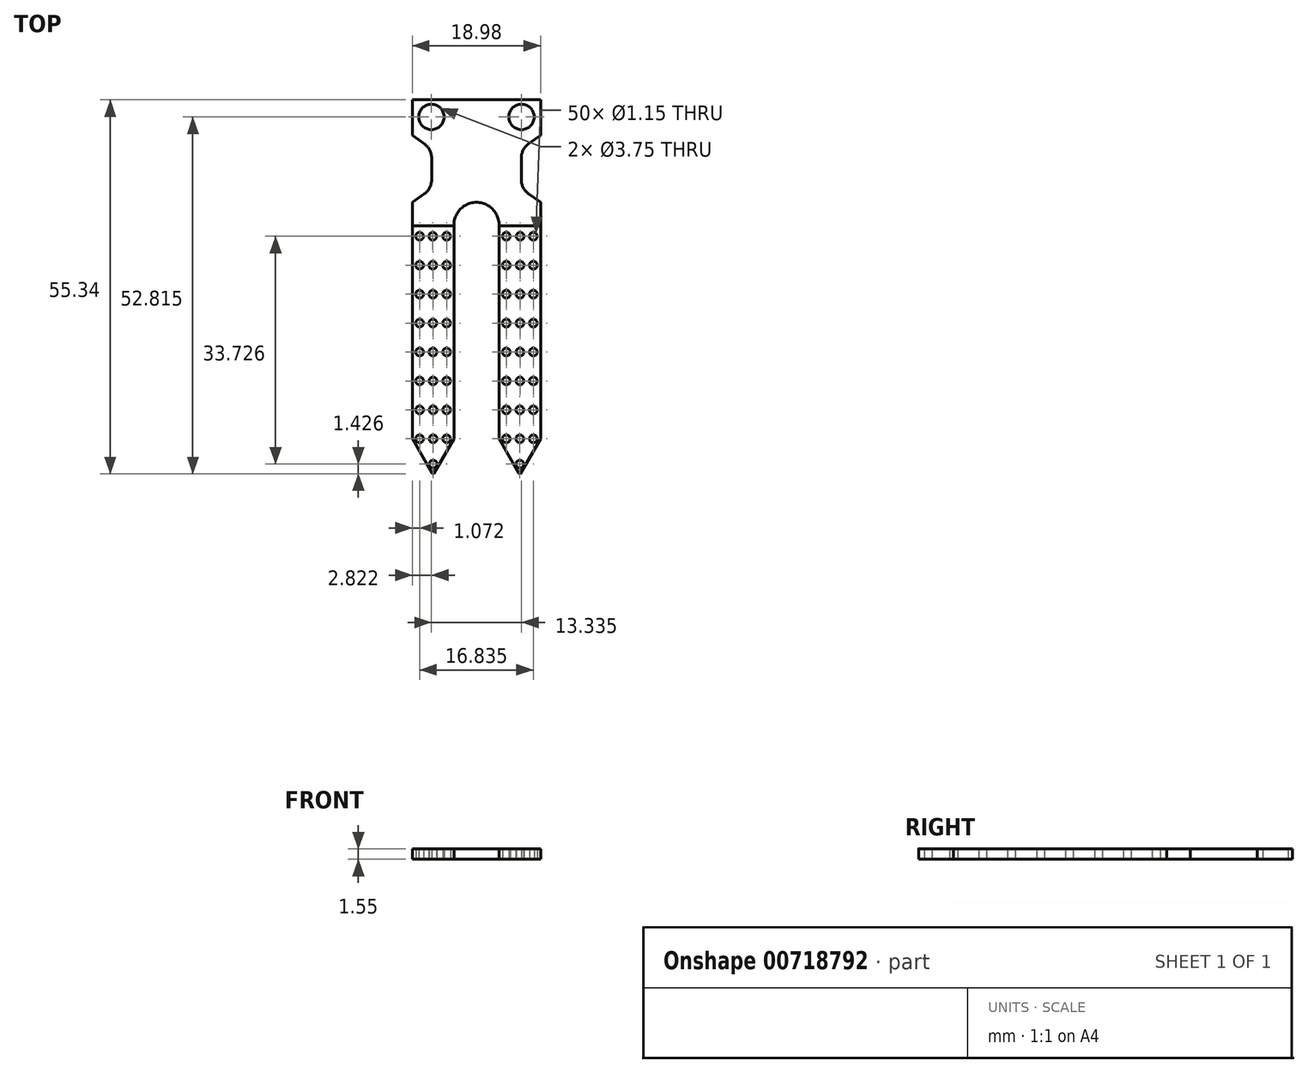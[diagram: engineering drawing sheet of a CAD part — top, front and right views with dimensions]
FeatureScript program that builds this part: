
annotation { "Feature Type Name" : "Feature", "Feature Type Description" : "" }
export const myFeature = defineFeature(function(context is Context, id is Id, definition is map)
    precondition{}
    {
        {
            var Q0;
            Q0=qCreatedBy(makeId("Top.planeOp"),FACE);
            var sketch = newSketch(context, id + "F0", { "sketchPlane" : qUnion([Q0])});
            skLineSegment(sketch, "E0", {"start": v(-9.5, 0) * mm, "end": v(9.5, 0) * mm});
            skLineSegment(sketch, "E1", {"start": v(9.5, 0) * mm, "end": v(9.5, -5.25) * mm});
            skLineSegment(sketch, "E2", {"start": v(9.5, -5.25) * mm, "end": v(6.64, -7.28) * mm});
            skLineSegment(sketch, "E3", {"start": v(6.64, -7.28) * mm, "end": v(6.64, -13.13) * mm});
            skLineSegment(sketch, "E4", {"start": v(6.64, -13.13) * mm, "end": v(9.5, -15.16) * mm});
            skLineSegment(sketch, "E5", {"start": v(9.5, -50.16) * mm, "end": v(6.42, -55.49) * mm});
            skLineSegment(sketch, "E6", {"start": v(6.42, -55.49) * mm, "end": v(3.34, -50.16) * mm});
            skLineSegment(sketch, "E7", {"start": v(9.5, -50.16) * mm, "end": v(3.34, -50.16) * mm, "construction": true});
            skLineSegment(sketch, "E8", {"start": v(6.42, -55.49) * mm, "end": v(6.42, -50.16) * mm, "construction": true});
            skLineSegment(sketch, "E9", {"start": v(9.5, -15.16) * mm, "end": v(9.5, -18.61) * mm});
            skLineSegment(sketch, "E10", {"start": v(9.5, -18.61) * mm, "end": v(9.5, -50.16) * mm});
            skLineSegment(sketch, "E11", {"start": v(3.34, -50.16) * mm, "end": v(3.34, -18.61) * mm});
            skLineSegment(sketch, "E12", {"start": v(3.34, -18.61) * mm, "end": v(9.5, -18.61) * mm});
            skLineSegment(sketch, "E13", {"start": v(0, 0) * mm, "end": v(0, -55.81) * mm, "construction": true});
            skLineSegment(sketch, "E14.MirrorCS", {"start": v(-9.5, -15.16) * mm, "end": v(-9.5, -18.61) * mm});
            skLineSegment(sketch, "E15.MirrorCS", {"start": v(-9.5, -18.61) * mm, "end": v(-9.5, -50.16) * mm});
            skLineSegment(sketch, "E16.MirrorCS", {"start": v(-6.64, -7.28) * mm, "end": v(-6.64, -13.13) * mm});
            skLineSegment(sketch, "E17.MirrorCS", {"start": v(-9.5, -5.25) * mm, "end": v(-6.64, -7.28) * mm});
            skLineSegment(sketch, "E18.MirrorCS", {"start": v(-9.5, 0) * mm, "end": v(-9.5, -5.25) * mm});
            skLineSegment(sketch, "E19.MirrorCS", {"start": v(-6.64, -13.13) * mm, "end": v(-9.5, -15.16) * mm});
            skLineSegment(sketch, "E20.MirrorCS", {"start": v(-6.42, -55.49) * mm, "end": v(-3.34, -50.16) * mm});
            skLineSegment(sketch, "E21.MirrorCS", {"start": v(-9.5, -50.16) * mm, "end": v(-6.42, -55.49) * mm});
            skLineSegment(sketch, "E22.MirrorCS", {"start": v(-3.34, -50.16) * mm, "end": v(-3.34, -18.61) * mm});
            skLineSegment(sketch, "E23.MirrorCS", {"start": v(-3.34, -18.61) * mm, "end": v(-9.5, -18.61) * mm});
            skLineSegment(sketch, "E24", {"start": v(-3.34, -18.61) * mm, "end": v(3.34, -18.61) * mm, "construction": true});
            skLineSegment(sketch, "E25", {"start": v(-9.5, -15.16) * mm, "end": v(9.5, -15.16) * mm, "construction": true});
            skArc(sketch, "E26", {"start": v(3.34, -18.61) * mm, "mid": v(0, -15.16) * mm, "end": v(-3.34, -18.61) * mm});
            skLineSegment(sketch, "E27.MirrorCS", {"start": v(-9.5, -50.16) * mm, "end": v(-3.34, -50.16) * mm, "construction": true});
            skLineSegment(sketch, "E28.MirrorCS", {"start": v(-6.42, -55.49) * mm, "end": v(-6.42, -50.16) * mm, "construction": true});
            skCircle(sketch, "E29", {"center": v(6.67, -2.52) * mm, "radius": 1.88 * mm});
            skCircle(sketch, "E30.MirrorC", {"center": v(-6.67, -2.52) * mm, "radius": 1.88 * mm});
            skCircle(sketch, "E31", {"center": v(4.42, -20.19) * mm, "radius": 0.57 * mm});
            skCircle(sketch, "E32", {"center": v(6.47, -20.19) * mm, "radius": 0.57 * mm});
            skCircle(sketch, "E33", {"center": v(8.42, -20.19) * mm, "radius": 0.57 * mm});
            skLineSegment(sketch, "E34", {"start": v(3.34, -20.19) * mm, "end": v(9.5, -20.19) * mm, "construction": true});
            skCircle(sketch, "E35", {"center": v(6.42, -53.91) * mm, "radius": 0.57 * mm});
            skCircle(sketch, "E36", {"center": v(4.42, -50.16) * mm, "radius": 0.57 * mm});
            skCircle(sketch, "E37", {"center": v(6.42, -50.16) * mm, "radius": 0.57 * mm});
            skCircle(sketch, "E38", {"center": v(8.42, -50.16) * mm, "radius": 0.57 * mm});
            skLineSegment(sketch, "E39", {"start": v(4.42, -50.16) * mm, "end": v(4.42, -20.19) * mm, "construction": true});
            skLineSegment(sketch, "E40", {"start": v(6.42, -50.16) * mm, "end": v(6.47, -20.19) * mm, "construction": true});
            skLineSegment(sketch, "E41", {"start": v(8.42, -20.19) * mm, "end": v(8.42, -50.16) * mm, "construction": true});
            skLineSegment(sketch, "E42", {"start": v(3.34, -41.6) * mm, "end": v(9.5, -41.6) * mm, "construction": true});
            skLineSegment(sketch, "E43", {"start": v(3.34, -37.32) * mm, "end": v(9.5, -37.32) * mm, "construction": true});
            skLineSegment(sketch, "E44", {"start": v(3.34, -33.03) * mm, "end": v(9.5, -33.03) * mm, "construction": true});
            skLineSegment(sketch, "E45", {"start": v(3.34, -28.75) * mm, "end": v(9.5, -28.75) * mm, "construction": true});
            skLineSegment(sketch, "E46", {"start": v(3.34, -24.47) * mm, "end": v(9.5, -24.47) * mm, "construction": true});
            skCircle(sketch, "E47", {"center": v(4.42, -24.47) * mm, "radius": 0.57 * mm});
            skCircle(sketch, "E48", {"center": v(6.46, -24.47) * mm, "radius": 0.57 * mm});
            skCircle(sketch, "E49", {"center": v(8.42, -24.47) * mm, "radius": 0.57 * mm});
            skCircle(sketch, "E50", {"center": v(4.42, -28.75) * mm, "radius": 0.57 * mm});
            skCircle(sketch, "E51", {"center": v(6.45, -28.75) * mm, "radius": 0.57 * mm});
            skCircle(sketch, "E52", {"center": v(8.42, -28.75) * mm, "radius": 0.57 * mm});
            skLineSegment(sketch, "E53", {"start": v(3.34, -45.88) * mm, "end": v(9.5, -45.88) * mm, "construction": true});
            skCircle(sketch, "E54", {"center": v(4.42, -33.03) * mm, "radius": 0.57 * mm});
            skCircle(sketch, "E55", {"center": v(6.45, -33.03) * mm, "radius": 0.57 * mm});
            skCircle(sketch, "E56", {"center": v(8.42, -33.03) * mm, "radius": 0.57 * mm});
            skCircle(sketch, "E57", {"center": v(4.42, -37.32) * mm, "radius": 0.57 * mm});
            skCircle(sketch, "E58", {"center": v(6.44, -37.32) * mm, "radius": 0.57 * mm});
            skCircle(sketch, "E59", {"center": v(8.42, -37.32) * mm, "radius": 0.57 * mm});
            skCircle(sketch, "E60", {"center": v(4.42, -41.6) * mm, "radius": 0.57 * mm});
            skCircle(sketch, "E61", {"center": v(6.43, -41.6) * mm, "radius": 0.57 * mm});
            skCircle(sketch, "E62", {"center": v(8.42, -41.6) * mm, "radius": 0.57 * mm});
            skCircle(sketch, "E63", {"center": v(4.42, -45.88) * mm, "radius": 0.57 * mm});
            skCircle(sketch, "E64", {"center": v(6.42, -45.88) * mm, "radius": 0.57 * mm});
            skCircle(sketch, "E65", {"center": v(8.42, -45.88) * mm, "radius": 0.57 * mm});
            skCircle(sketch, "E66.MirrorC", {"center": v(-4.42, -20.19) * mm, "radius": 0.57 * mm});
            skCircle(sketch, "E67.MirrorC", {"center": v(-8.42, -33.03) * mm, "radius": 0.57 * mm});
            skCircle(sketch, "E68.MirrorC", {"center": v(-4.42, -37.32) * mm, "radius": 0.57 * mm});
            skCircle(sketch, "E69.MirrorC", {"center": v(-6.46, -24.47) * mm, "radius": 0.57 * mm});
            skCircle(sketch, "E70.MirrorC", {"center": v(-6.47, -20.19) * mm, "radius": 0.57 * mm});
            skCircle(sketch, "E71.MirrorC", {"center": v(-6.45, -33.03) * mm, "radius": 0.57 * mm});
            skCircle(sketch, "E72.MirrorC", {"center": v(-4.42, -28.75) * mm, "radius": 0.57 * mm});
            skCircle(sketch, "E73.MirrorC", {"center": v(-6.42, -45.88) * mm, "radius": 0.57 * mm});
            skLineSegment(sketch, "E74.MirrorCS", {"start": v(-8.42, -20.19) * mm, "end": v(-8.42, -50.16) * mm, "construction": true});
            skCircle(sketch, "E75.MirrorC", {"center": v(-8.42, -41.6) * mm, "radius": 0.57 * mm});
            skLineSegment(sketch, "E76.MirrorCS", {"start": v(-3.34, -24.47) * mm, "end": v(-9.5, -24.47) * mm, "construction": true});
            skLineSegment(sketch, "E77.MirrorCS", {"start": v(-3.34, -45.88) * mm, "end": v(-9.5, -45.88) * mm, "construction": true});
            skCircle(sketch, "E78.MirrorC", {"center": v(-8.42, -50.16) * mm, "radius": 0.57 * mm});
            skCircle(sketch, "E79.MirrorC", {"center": v(-4.42, -24.47) * mm, "radius": 0.57 * mm});
            skLineSegment(sketch, "E80.MirrorCS", {"start": v(-3.34, -20.19) * mm, "end": v(-9.5, -20.19) * mm, "construction": true});
            skCircle(sketch, "E81.MirrorC", {"center": v(-8.42, -45.88) * mm, "radius": 0.57 * mm});
            skLineSegment(sketch, "E82.MirrorCS", {"start": v(-6.42, -50.16) * mm, "end": v(-6.47, -20.19) * mm, "construction": true});
            skCircle(sketch, "E83.MirrorC", {"center": v(-4.42, -33.03) * mm, "radius": 0.57 * mm});
            skCircle(sketch, "E84.MirrorC", {"center": v(-8.42, -20.19) * mm, "radius": 0.57 * mm});
            skCircle(sketch, "E85.MirrorC", {"center": v(-6.42, -50.16) * mm, "radius": 0.57 * mm});
            skCircle(sketch, "E86.MirrorC", {"center": v(-8.42, -28.75) * mm, "radius": 0.57 * mm});
            skCircle(sketch, "E87.MirrorC", {"center": v(-8.42, -37.32) * mm, "radius": 0.57 * mm});
            skLineSegment(sketch, "E88.MirrorCS", {"start": v(-3.34, -33.03) * mm, "end": v(-9.5, -33.03) * mm, "construction": true});
            skCircle(sketch, "E89.MirrorC", {"center": v(-8.42, -24.47) * mm, "radius": 0.57 * mm});
            skCircle(sketch, "E90.MirrorC", {"center": v(-6.44, -37.32) * mm, "radius": 0.57 * mm});
            skCircle(sketch, "E91.MirrorC", {"center": v(-6.43, -41.6) * mm, "radius": 0.57 * mm});
            skCircle(sketch, "E92.MirrorC", {"center": v(-4.42, -50.16) * mm, "radius": 0.57 * mm});
            skLineSegment(sketch, "E93.MirrorCS", {"start": v(-3.34, -41.6) * mm, "end": v(-9.5, -41.6) * mm, "construction": true});
            skCircle(sketch, "E94.MirrorC", {"center": v(-4.42, -45.88) * mm, "radius": 0.57 * mm});
            skLineSegment(sketch, "E95.MirrorCS", {"start": v(-3.34, -37.32) * mm, "end": v(-9.5, -37.32) * mm, "construction": true});
            skCircle(sketch, "E96.MirrorC", {"center": v(-4.42, -41.6) * mm, "radius": 0.57 * mm});
            skLineSegment(sketch, "E97.MirrorCS", {"start": v(-3.34, -28.75) * mm, "end": v(-9.5, -28.75) * mm, "construction": true});
            skLineSegment(sketch, "E98.MirrorCS", {"start": v(-4.42, -50.16) * mm, "end": v(-4.42, -20.19) * mm, "construction": true});
            skCircle(sketch, "E99.MirrorC", {"center": v(-6.45, -28.75) * mm, "radius": 0.57 * mm});
            skCircle(sketch, "E100.MirrorC", {"center": v(-6.42, -53.91) * mm, "radius": 0.57 * mm});
            skSolve(sketch);
        }
        {
            var Q0;
            Q0=makeQuery(id+"F0.imprint","IMPRINT",FACE,{"disambiguationData":[TD([[makeQuery(id+"F0.imprint","IMPRINT",EDGE,{"derivedFrom":sQuery(id+"F0.wireOp",EDGE,"E0")}),-1.0]])]});
            extrude(context, id + "F1", {"entities" : qUnion([Q0]), "depth" : 1.55 * mm, "offsetDistance" : 25 * mm});
        }
        {
            var Q0;
            Q0=makeQuery(id+"F0.imprint","IMPRINT",FACE,{"disambiguationData":[TD([[makeQuery(id+"F0.imprint","IMPRINT",EDGE,{"derivedFrom":sQuery(id+"F0.wireOp",EDGE,"E15.MirrorCS")}),1.0]])]});
            var Q1;
            Q1=makeQuery(id+"F0.imprint","IMPRINT",FACE,{"disambiguationData":[TD([[makeQuery(id+"F0.imprint","IMPRINT",EDGE,{"derivedFrom":sQuery(id+"F0.wireOp",EDGE,"E5")}),-1.0]])]});
            extrude(context, id + "F2", {"entities" : qUnion([Q0, Q1]), "depth" : 1.55 * mm, "offsetDistance" : 25 * mm});
        }
        {
            var Q0;
            Q0=makeQuery(id+"F2.opExtrude","SWEPT_EDGE",EDGE,{"disambiguationData":[OSD([sQuery(id+"F0.wireOp",EDGE,"E5"),sQuery(id+"F0.wireOp",EDGE,"E6")])]});
            var Q1;
            Q1=makeQuery(id+"F2.opExtrude","SWEPT_EDGE",EDGE,{"disambiguationData":[OSD([sQuery(id+"F0.wireOp",EDGE,"E21.MirrorCS"),sQuery(id+"F0.wireOp",EDGE,"E20.MirrorCS")])]});
            fillet(context, id + "F3", {"entities" : qUnion([Q0, Q1]), "radius" : .15 * mm, "tangentPropagation" : true, "allowEdgeOverflow" : false});
        }
        {
            var Q0;
            Q0=makeQuery(id+"F1.opExtrude","SWEPT_EDGE",EDGE,{"disambiguationData":[OSD([sQuery(id+"F0.wireOp",EDGE,"E16.MirrorCS"),sQuery(id+"F0.wireOp",EDGE,"E17.MirrorCS")])]});
            var Q1;
            Q1=makeQuery(id+"F1.opExtrude","SWEPT_EDGE",EDGE,{"disambiguationData":[OSD([sQuery(id+"F0.wireOp",EDGE,"E16.MirrorCS"),sQuery(id+"F0.wireOp",EDGE,"E19.MirrorCS")])]});
            var Q2;
            Q2=makeQuery(id+"F1.opExtrude","SWEPT_EDGE",EDGE,{"disambiguationData":[OSD([sQuery(id+"F0.wireOp",EDGE,"E3"),sQuery(id+"F0.wireOp",EDGE,"E4")])]});
            var Q3;
            Q3=makeQuery(id+"F1.opExtrude","SWEPT_EDGE",EDGE,{"disambiguationData":[OSD([sQuery(id+"F0.wireOp",EDGE,"E2"),sQuery(id+"F0.wireOp",EDGE,"E3")])]});
            fillet(context, id + "F4", {"entities" : qUnion([Q0, Q1, Q2, Q3]), "radius" : 2.5 * mm, "tangentPropagation" : true, "allowEdgeOverflow" : false});
        }
    });
